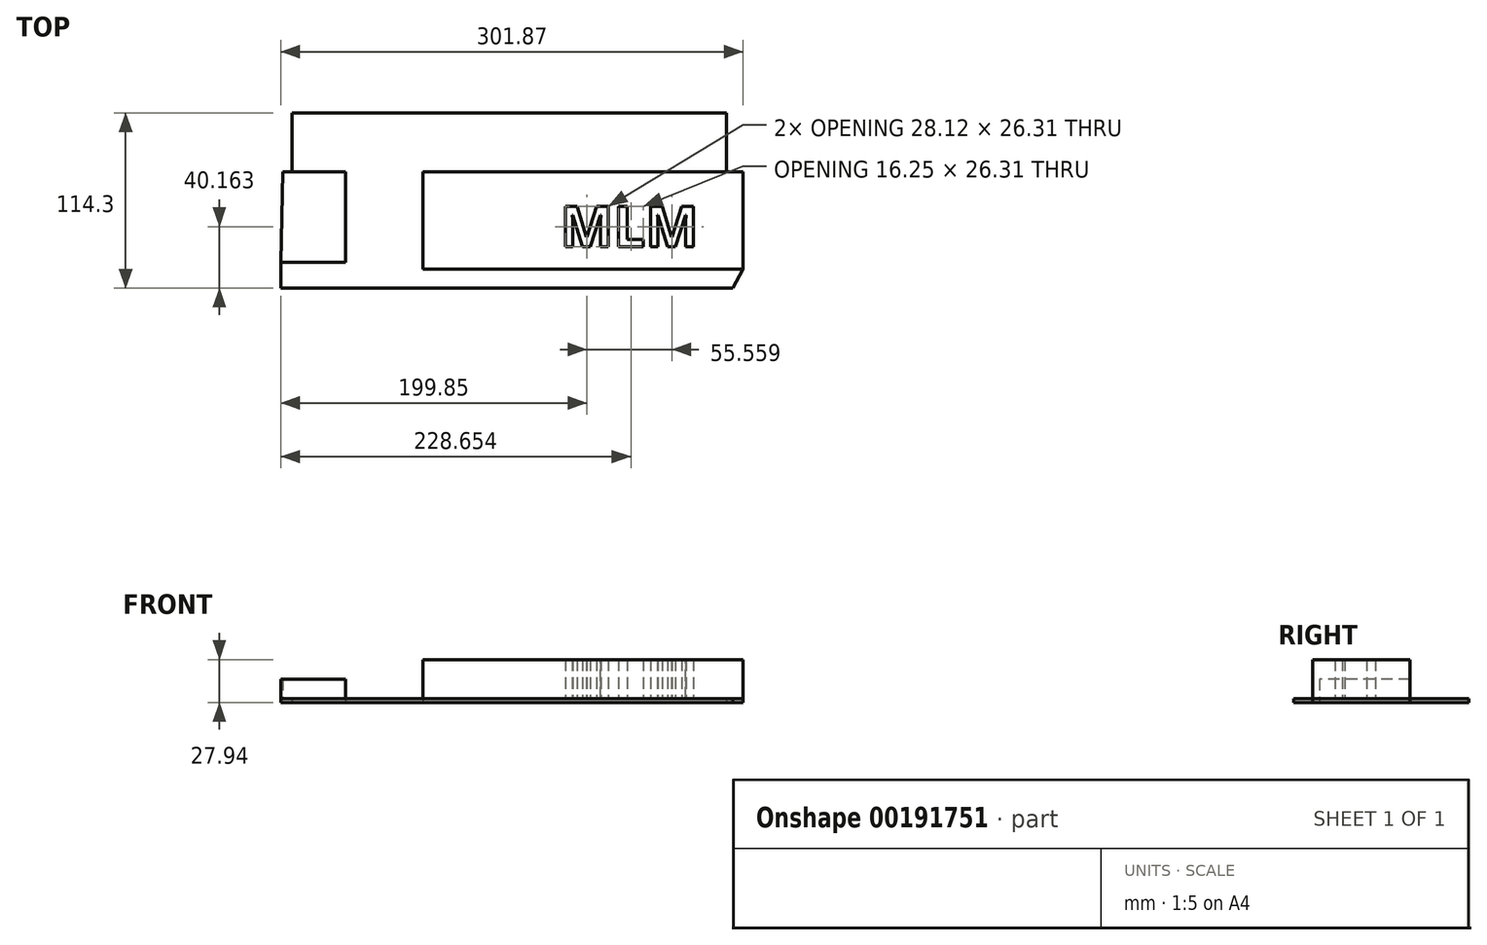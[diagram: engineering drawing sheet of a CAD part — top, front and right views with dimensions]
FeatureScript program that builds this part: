
annotation { "Feature Type Name" : "Feature", "Feature Type Description" : "" }
export const myFeature = defineFeature(function(context is Context, id is Id, definition is map)
    precondition{}
    {
        {
            var Q0;
            Q0=qCreatedBy(makeId("Top.planeOp"),FACE);
            var sketch = newSketch(context, id + "F0", { "sketchPlane" : qUnion([Q0])});
            skLineSegment(sketch, "E0", {"start": v(-150.54, -53.54) * mm, "end": v(-150.54, -36.73) * mm});
            skLineSegment(sketch, "E1", {"start": v(-150.54, -36.73) * mm, "end": v(-108.2, -36.73) * mm});
            skLineSegment(sketch, "E2", {"start": v(-108.2, -36.73) * mm, "end": v(-108.2, 22.4) * mm});
            skLineSegment(sketch, "E3", {"start": v(-108.2, 22.4) * mm, "end": v(-142.99, 22.4) * mm});
            skLineSegment(sketch, "E4", {"start": v(-142.99, 22.4) * mm, "end": v(-142.99, 60.76) * mm});
            skLineSegment(sketch, "E5", {"start": v(-142.99, 60.76) * mm, "end": v(140.27, 60.76) * mm});
            skLineSegment(sketch, "E6", {"start": v(140.27, 60.76) * mm, "end": v(140.27, 22.4) * mm});
            skLineSegment(sketch, "E7", {"start": v(140.27, 22.4) * mm, "end": v(-57.7, 22.4) * mm});
            skLineSegment(sketch, "E8", {"start": v(-57.7, 22.4) * mm, "end": v(-57.7, -41.1) * mm});
            skLineSegment(sketch, "E9", {"start": v(-57.7, -41.1) * mm, "end": v(151.33, -41.1) * mm});
            skLineSegment(sketch, "E10", {"start": v(151.33, -41.1) * mm, "end": v(144.63, -53.54) * mm});
            skLineSegment(sketch, "E11", {"start": v(144.63, -53.54) * mm, "end": v(-150.54, -53.54) * mm});
            skSolve(sketch);
        }
        {
            var Q0;
            Q0 = qSketchRegion(id + "F0", true);
            extrude(context, id + "F1", {"entities" : qUnion([Q0]), "depth" : 2.54 * mm});
        }
        {
            var Q0;
            Q0=makeQuery(id+"F1.opExtrude","CAP_FACE",FACE,{"disambiguationData":[OSD([sQuery(id+"F0.wireOp",EDGE,"E0"),sQuery(id+"F0.wireOp",EDGE,"E1"),sQuery(id+"F0.wireOp",EDGE,"E2"),sQuery(id+"F0.wireOp",EDGE,"E3"),sQuery(id+"F0.wireOp",EDGE,"E4"),sQuery(id+"F0.wireOp",EDGE,"E5"),sQuery(id+"F0.wireOp",EDGE,"E6"),sQuery(id+"F0.wireOp",EDGE,"E7"),sQuery(id+"F0.wireOp",EDGE,"E8"),sQuery(id+"F0.wireOp",EDGE,"E9"),sQuery(id+"F0.wireOp",EDGE,"E10"),sQuery(id+"F0.wireOp",EDGE,"E11")])],"isStart":false});
            var sketch = newSketch(context, id + "F2", { "sketchPlane" : qUnion([Q0])});
            skLineSegment(sketch, "E12", {"start": v(-57.7, 22.4) * mm, "end": v(-57.7, -41.1) * mm});
            skLineSegment(sketch, "E13", {"start": v(-57.7, -41.1) * mm, "end": v(151.33, -41.1) * mm});
            skLineSegment(sketch, "E14", {"start": v(151.33, -41.1) * mm, "end": v(151.33, 22.4) * mm});
            skLineSegment(sketch, "E15", {"start": v(151.33, 22.4) * mm, "end": v(-57.7, 22.4) * mm});
            skText(sketch, "E16", { "text": "MLM", "fontName": "OpenSans-Bold.ttf"});
            const initialGuessF2  = {"E16": [0.03194, -0.02653, 1, 0, 0.02653]};
            skSetInitialGuess(sketch, initialGuessF2);
            skSolve(sketch);
        }
        {
            var Q0;
            Q0 = qSketchRegion(id + "F2", true);
            extrude(context, id + "F3", {"entities" : qUnion([Q0]), "depth" : 25.4 * mm});
        }
        {
            var Q0;
            Q0=makeQuery(id+"F1.opExtrude","CAP_FACE",FACE,{"disambiguationData":[OSD([sQuery(id+"F0.wireOp",EDGE,"E0"),sQuery(id+"F0.wireOp",EDGE,"E1"),sQuery(id+"F0.wireOp",EDGE,"E2"),sQuery(id+"F0.wireOp",EDGE,"E3"),sQuery(id+"F0.wireOp",EDGE,"E4"),sQuery(id+"F0.wireOp",EDGE,"E5"),sQuery(id+"F0.wireOp",EDGE,"E6"),sQuery(id+"F0.wireOp",EDGE,"E7"),sQuery(id+"F0.wireOp",EDGE,"E8"),sQuery(id+"F0.wireOp",EDGE,"E9"),sQuery(id+"F0.wireOp",EDGE,"E10"),sQuery(id+"F0.wireOp",EDGE,"E11")])],"isStart":false});
            var sketch = newSketch(context, id + "F4", { "sketchPlane" : qUnion([Q0])});
            skLineSegment(sketch, "E17", {"start": v(-136.16, 22.4) * mm, "end": v(-149.2, 22.4) * mm});
            skLineSegment(sketch, "E18", {"start": v(-149.2, 22.4) * mm, "end": v(-150.54, -36.73) * mm});
            skLineSegment(sketch, "E19", {"start": v(-150.54, -36.73) * mm, "end": v(-108.2, -36.73) * mm});
            skLineSegment(sketch, "E20", {"start": v(-108.2, -36.73) * mm, "end": v(-108.2, 22.4) * mm});
            skLineSegment(sketch, "E21", {"start": v(-108.2, 22.4) * mm, "end": v(-136.16, 22.4) * mm});
            skSolve(sketch);
        }
        {
            var Q0;
            Q0 = qSketchRegion(id + "F4", true);
            extrude(context, id + "F5", {"entities" : qUnion([Q0]), "depth" : 12.7 * mm});
        }
    });
